# Revit family: CADS_Vent-Axia_MechEquip_Fan_VSP_SabreSicklePlate_3Ph6P - EXTRACT
name_source: partatom
category: Mechanical Equipment
units: mm (PartAtom-declared; Revit-internal decimal feet)

## family parameters
Always vertical = Yes
Cut with Voids When Loaded = No
OmniClass Number = 23.75.00.00
OmniClass Title = Climate Control (HVAC)
Part Type = Normal
Room Calculation Point = No
Round Connector Dimension = Use Diameter
Shared = No
Work Plane-Based = No

## types (4) — shared parameters
AirflowRateRange = 0.0 L/s
AssemblyPlace = UNKNOWN
AssetType = FIXED
DurationUnit = Year
E = 34 mm
ExteriorInsulation = No
Fitting Type = Ignore
G = 17 mm
GrossWeight = 0.00 kg
HasProtectiveEarth = No
IfcExportAs = IfcFanType
IsExtendedWarranty = No
ManufacturerAddress = Fleming Way
Crawley 
RH10 9YX
Quantity = 1
RatedCurrent = 0 A
RatedVoltage = 0 V
Status = New
WarrantyGuarantor = Vent-Axia Limited
WorkingPressure = 0.0 Pa
zero-valued in all types: CADS_Index, CADS_Usage, Default Elevation, ExpectedServiceLife, NumberOfPoles

## per-type parameters (varying)
| type | A | ModelReference | NominalDiameter | NominalHeight | NominalLength | NominalWidth |
| VSP50036A | 725 mm  [stored 2.37861 ft] | OWLET SICKLE PLATE FAN 500 DIA 3PH 6 POLE | 500 mm  [stored 1.64042 ft] | 500 mm  [stored 1.64042 ft] | 142 mm | 725 mm  [stored 2.37861 ft] |
| VSP56036 | 725 mm  [stored 2.37861 ft] | SICKLE PLATE FAN 560DIA 3PH 6 POLE | 560 mm  [stored 1.83727 ft] | 560 mm  [stored 1.83727 ft] | 163 mm | 725 mm  [stored 2.37861 ft] |
| VSP63036B | 805 mm  [stored 2.64108 ft] | 630MM 3PH 6P PLATE FAN | 630 mm  [stored 2.06693 ft] | 630 mm  [stored 2.06693 ft] | 160 mm | 805 mm  [stored 2.64108 ft] |
| VSP71036A | 850 mm  [stored 2.78871 ft] | OWLET SICKLE PLATE FAN 710 DIA 3 PH 6 POLE | 710 mm | 710 mm | 202 mm | 850 mm  [stored 2.78871 ft] |

note: column(s) folded — value = type name in every type: ModelNumber

note: [stored X ft] marks values corroborated as IEEE doubles in the binary element streams (Revit-internal decimal feet)

## geometry (parser evidence)
native form markers: Sweep x14
no freeform markers — native parametric forms only
